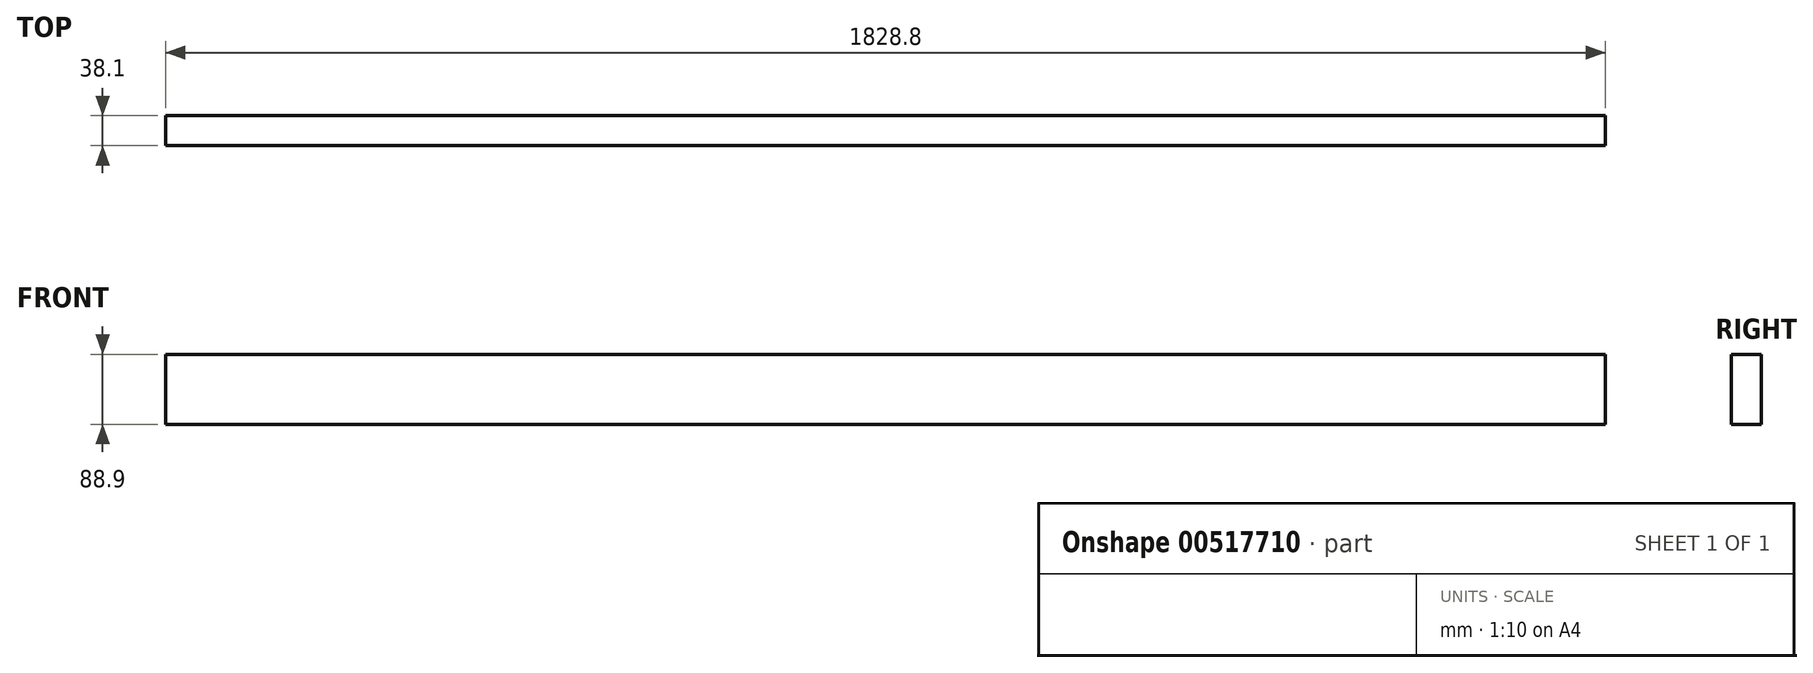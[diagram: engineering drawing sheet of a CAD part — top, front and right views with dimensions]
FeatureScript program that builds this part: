
annotation { "Feature Type Name" : "Feature", "Feature Type Description" : "" }
export const myFeature = defineFeature(function(context is Context, id is Id, definition is map)
    precondition{}
    {
        {
            var Q0;
            Q0=qCreatedBy(makeId("Front.planeOp"),FACE);
            var sketch = newSketch(context, id + "F0", { "sketchPlane" : qUnion([Q0])});
            skLineSegment(sketch, "E0.bottom", {"start": v(914.4, 44.45) * mm, "end": v(-914.4, 44.45) * mm});
            skLineSegment(sketch, "E0.top", {"start": v(914.4, -44.45) * mm, "end": v(-914.4, -44.45) * mm});
            skLineSegment(sketch, "E0.left", {"start": v(914.4, 44.45) * mm, "end": v(914.4, -44.45) * mm});
            skLineSegment(sketch, "E0.right", {"start": v(-914.4, 44.45) * mm, "end": v(-914.4, -44.45) * mm});
            skPoint(sketch, "E0.middle", {"position": v(0, 0) * mm});
            skSolve(sketch);
        }
        {
            var Q0;
            Q0=makeQuery(id+"F0.imprint","IMPRINT",FACE,{"disambiguationData":[TD([[makeQuery(id+"F0.imprint","IMPRINT",EDGE,{"derivedFrom":sQuery(id+"F0.wireOp",EDGE,"E0.bottom")}),1.0]])]});
            extrude(context, id + "F1", {"entities" : qUnion([Q0]), "depth" : 38.1 * mm, "offsetDistance" : 25.4 * mm});
        }
    });
